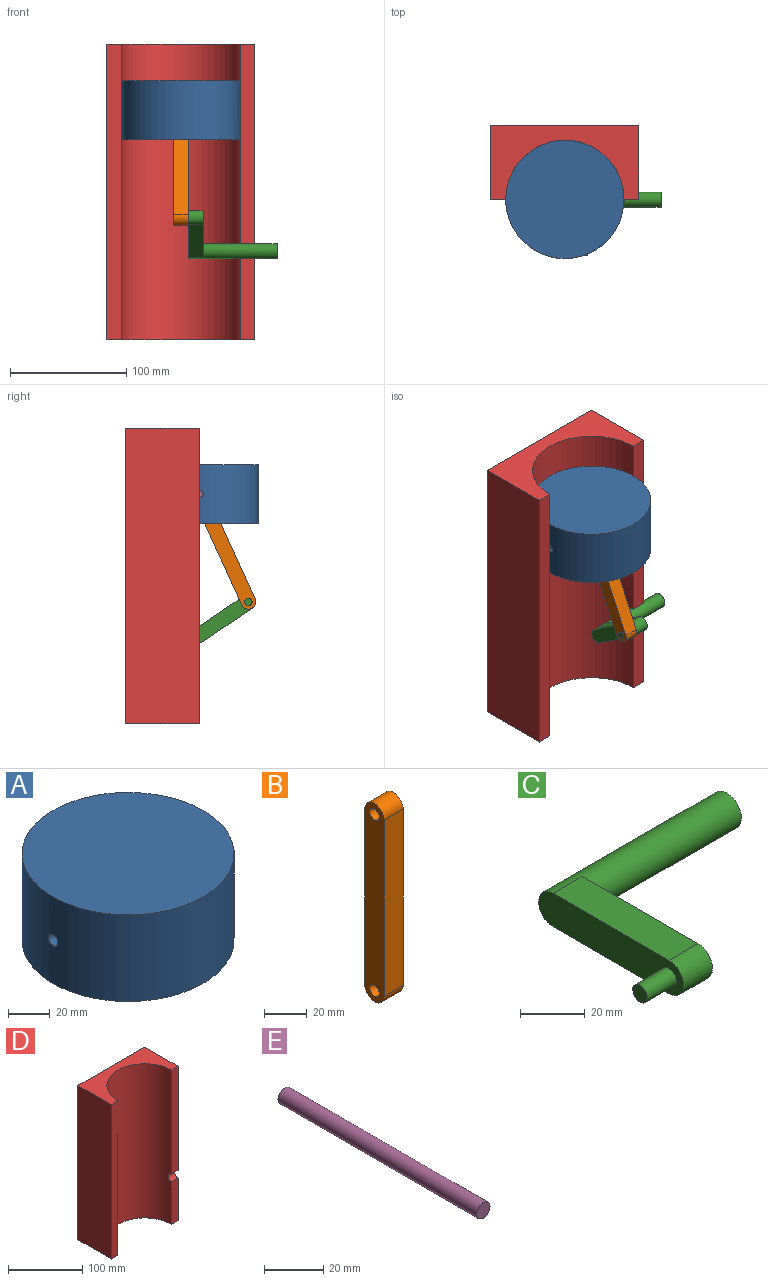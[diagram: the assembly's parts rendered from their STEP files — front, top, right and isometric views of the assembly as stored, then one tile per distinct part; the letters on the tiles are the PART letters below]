
ASSEMBLY  parts=5 mates=5
PART A: 7 faces, bbox 101.6x101.6x50.8 mm
  f0: cylinder r=50.8mm len=101.6mm, axis (0,0,1), area 16151.3mm2, adj f2,f3,f5,f6
  f1: cylinder r=44.45mm len=88.9mm, axis (0,0,1), area 12351mm2, adj f2,f4,f5,f6
  f2: plane 101.6x101.6mm, normal (0,0,-1), area 1900.2mm2, adj f0,f1
  f3: plane 101.6x101.6mm, normal (0,0,1), area 8107.3mm2, adj f0
  f4: plane 88.9x88.9mm, normal (0,0,-1), area 6207.2mm2, adj f1
  f5: cylinder r=3.17mm len=6.46mm, axis (1,0,0), area 126.8mm2, adj f0,f1
  f6: cylinder r=3.17mm len=6.46mm, axis (-1,0,0), area 126.8mm2, adj f0,f1
PART B: 8 faces, bbox 12.7x12.7x114.3 mm
  f0: plane 101.6x12.7mm, normal (0,1,0), area 1290.3mm2, adj f1,f3,f4,f5
  f1: cylinder r=6.35mm len=12.7mm, axis (-1,0,0), area 253.4mm2, adj f0,f2,f4,f5
  f2: plane 101.6x12.7mm, normal (0,-1,0), area 1290.3mm2, adj f1,f3,f4,f5
  f3: cylinder r=6.35mm len=12.7mm, axis (-1,0,0), area 253.4mm2, adj f0,f2,f4,f5
  f4: plane 114.3x12.7mm, normal (1,0,0), area 1353.7mm2, adj f0,f1,f2,f3,f6,f7
  f5: plane 114.3x12.7mm, normal (-1,0,0), area 1353.7mm2, adj f0,f1,f2,f3,f6,f7
  f6: cylinder r=3.17mm len=12.7mm, axis (1,0,0), area 253.4mm2, adj f4,f5
  f7: cylinder r=3.17mm len=12.7mm, axis (1,0,0), area 253.4mm2, adj f4,f5
PART C: 9 faces, bbox 88.9x63.5x12.7 mm
  f0: cylinder r=6.35mm len=12.7mm, axis (-1,0,0), area 253.4mm2, adj f1,f3,f4,f5
  f1: plane 50.8x12.7mm, normal (0,0,-1), area 645.2mm2, adj f0,f2,f4,f5
  f2: cylinder r=6.35mm len=76.2mm, axis (-1,0,0), area 2786.9mm2, adj f1,f3,f4,f5,f8
  f3: plane 50.8x12.7mm, normal (0,0,1), area 645.2mm2, adj f0,f2,f4,f5
  f4: plane 57.15x12.7mm, normal (1,0,0), area 645.2mm2, adj f0,f1,f2,f3
  f5: plane 63.5x12.7mm, normal (-1,0,0), area 740.2mm2, adj f0,f1,f2,f3,f6
  f6: cylinder r=3.17mm len=12.7mm, axis (1,0,0), area 253.4mm2, adj f5,f7
  f7: plane 6.35x6.35mm, normal (-1,0,0), area 31.7mm2, adj f6
  f8: plane 12.7x12.7mm, normal (1,0,0), area 126.7mm2, adj f2
PART D: 11 faces, bbox 127x63.5x254 mm
  f0: cylinder r=50.8mm len=254mm, axis (0,0,1), area 40478.7mm2, adj f1,f2,f6,f7,f8,f9
  f1: plane 69.85x12.7mm, normal (0,-1,0), area 887.1mm2, adj f0,f3,f7,f10
  f2: plane 171.45x12.7mm, normal (0,-1,0), area 2177.4mm2, adj f0,f3,f8,f10
  f3: plane 254x63.5mm, normal (1,0,0), area 16065.7mm2, adj f1,f2,f4,f7,f8,f10
  f4: plane 254x127mm, normal (0,1,0), area 32258mm2, adj f3,f5,f7,f8
  f5: plane 254x63.5mm, normal (-1,0,0), area 16129mm2, adj f4,f6,f7,f8
  f6: plane 254x12.7mm, normal (0,-1,0), area 3225.8mm2, adj f0,f5,f7,f8
  f7: plane 127x63.5mm, normal (0,0,-1), area 4010.8mm2, adj f0,f1,f3,f4,f5,f6
  f8: plane 127x63.5mm, normal (0,0,1), area 4010.8mm2, adj f0,f2,f3,f4,f5,f6
  f9: cone r=0mm half-angle=59deg, axis (1,0,0), area 6.5mm2, adj f0,f10
  f10: cylinder r=6.35mm len=12.7mm, axis (1,0,0), area 253.4mm2, adj f1,f2,f3,f9
PART E: 3 faces, bbox 6.4x95.3x6.4 mm
  f0: cylinder r=3.17mm len=95.25mm, axis (0,1,0), area 1900.2mm2, adj f1,f2
  f1: plane 6.35x6.35mm, normal (0,-1,0), area 31.7mm2, adj f0
  f2: plane 6.35x6.35mm, normal (0,1,0), area 31.7mm2, adj f0
PLACE A t=(6.12,-50.73,-31.05)mm
PLACE B rot(axis=(-1,0,0),24.4deg) t=(-0.17,-71.74,-102.7)mm
PLACE C rot(axis=(-1,0,0),34.2deg) t=(12.53,-71.74,-163.22)mm
PLACE D t=(6.12,-50.73,0.31)mm fixed
PLACE E rot(axis=(-0.69,-0.69,-0.24),152.7deg) t=(6.18,-50.73,-56.45)mm
MATE slider A.f0 <-> D.f0  axis (0,0,1) through (6.12,-50.73,-56.45)mm
MATE revolute E.f0 <-> A.f5  axis (-1,0,0) through (-41.44,-50.73,-56.45)mm
MATE revolute B.f1 <-> E.f0  axis (1,0,0) through (6.18,-50.73,-56.45)mm
MATE revolute C.f6 <-> B.f3  axis (1,0,0) through (6.18,-92.75,-148.95)mm
MATE cylindrical C.f2 <-> D.f9  axis (-1,0,0) through (50.63,-50.73,-177.49)mm
